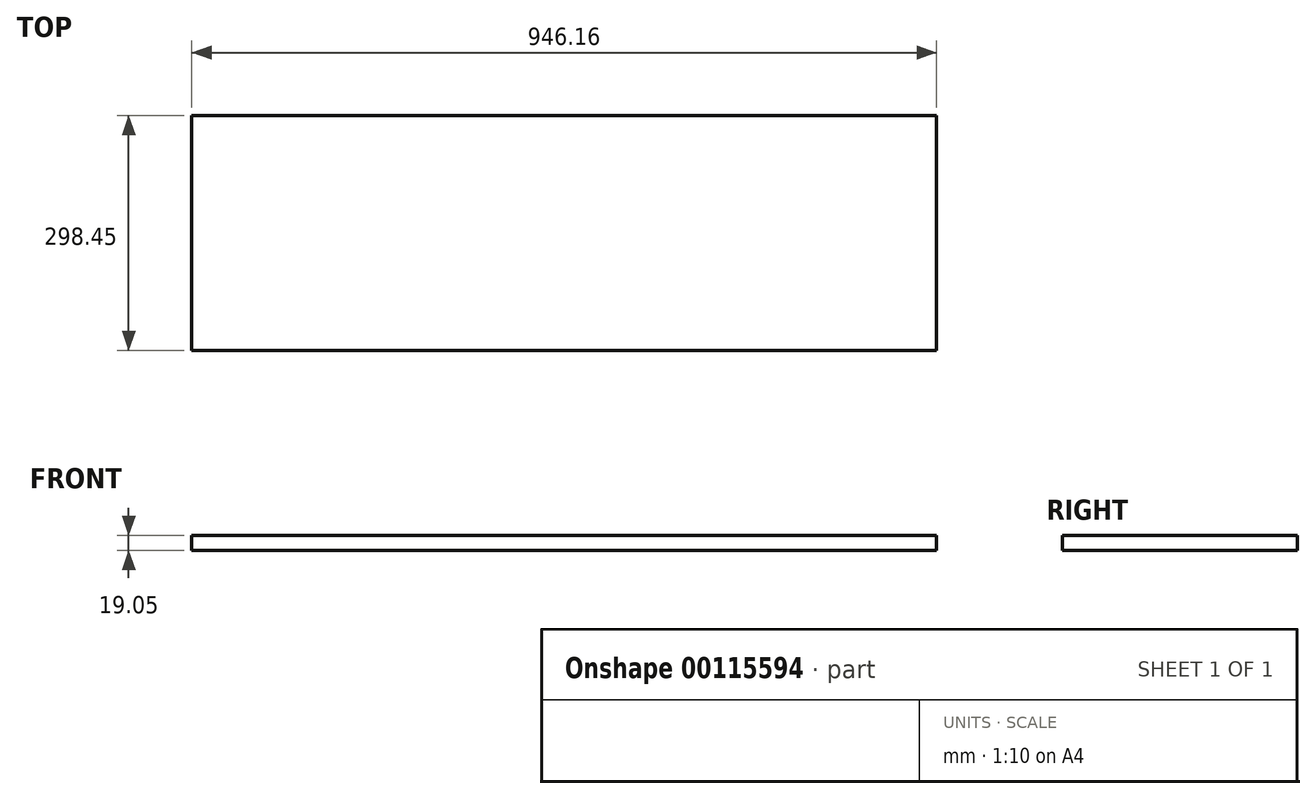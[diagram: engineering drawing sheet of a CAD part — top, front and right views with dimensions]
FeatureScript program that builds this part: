
annotation { "Feature Type Name" : "Feature", "Feature Type Description" : "" }
export const myFeature = defineFeature(function(context is Context, id is Id, definition is map)
    precondition{}
    {
        {
            var Q0;
            Q0=qCreatedBy(makeId("Front.planeOp"),FACE);
            var sketch = newSketch(context, id + "F0", { "sketchPlane" : qUnion([Q0])});
            skLineSegment(sketch, "E0.bottom", {"start": v(-473.08, 7.28) * mm, "end": v(473.07, 7.28) * mm});
            skLineSegment(sketch, "E0.top", {"start": v(-473.08, -11.77) * mm, "end": v(473.07, -11.77) * mm});
            skLineSegment(sketch, "E0.left", {"start": v(-473.08, 7.28) * mm, "end": v(-473.08, -11.77) * mm});
            skLineSegment(sketch, "E0.right", {"start": v(473.07, 7.28) * mm, "end": v(473.07, -11.77) * mm});
            skPoint(sketch, "E0.middle", {"position": v(0, -2.25) * mm});
            skSolve(sketch);
        }
        {
            var Q0;
            Q0=makeQuery(id+"F0.imprint","IMPRINT",FACE,{"disambiguationData":[TD([[makeQuery(id+"F0.imprint","IMPRINT",EDGE,{"derivedFrom":sQuery(id+"F0.wireOp",EDGE,"E0.bottom")}),-1.0]])]});
            extrude(context, id + "F1", {"entities" : qUnion([Q0]), "depth" : 298.45 * mm});
        }
    });
